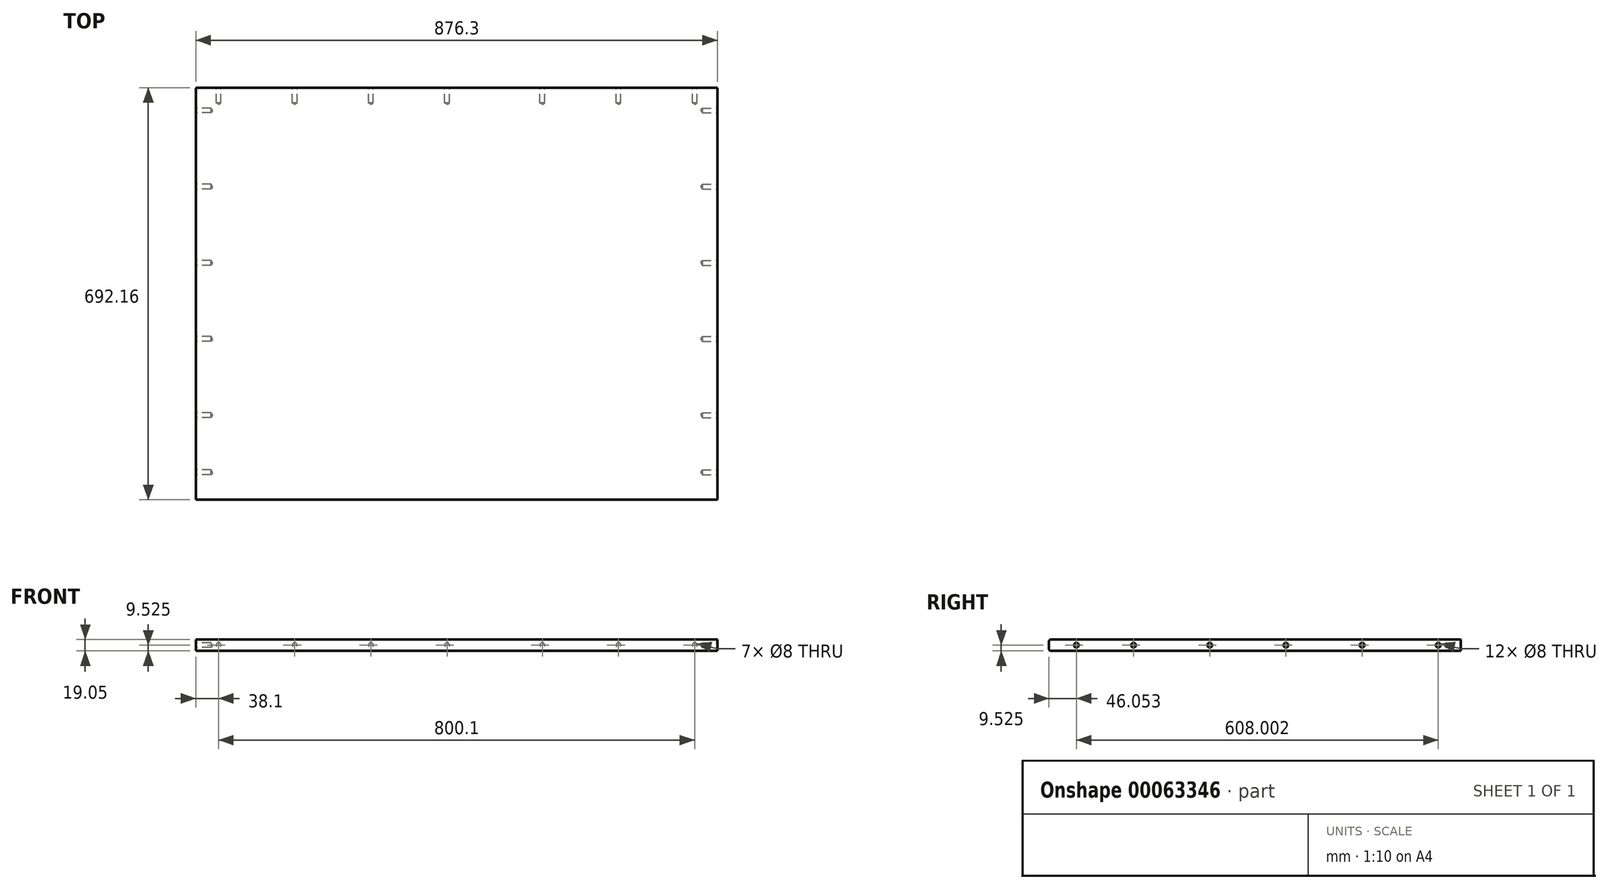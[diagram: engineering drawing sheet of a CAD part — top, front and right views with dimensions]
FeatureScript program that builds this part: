
annotation { "Feature Type Name" : "Feature", "Feature Type Description" : "" }
export const myFeature = defineFeature(function(context is Context, id is Id, definition is map)
    precondition{}
    {
        {
            var Q0;
            Q0=qCreatedBy(makeId("Top.planeOp"),FACE);
            var sketch = newSketch(context, id + "F0", { "sketchPlane" : qUnion([Q0])});
            skLineSegment(sketch, "E0.rect.bottom", {"start": v(438.15, -346.08) * mm, "end": v(-438.15, -346.08) * mm});
            skLineSegment(sketch, "E0.rect.top", {"start": v(438.15, 346.08) * mm, "end": v(-438.15, 346.07) * mm});
            skLineSegment(sketch, "E0.rect.left", {"start": v(438.15, -346.08) * mm, "end": v(438.15, 346.08) * mm});
            skLineSegment(sketch, "E0.rect.right", {"start": v(-438.15, -346.08) * mm, "end": v(-438.15, 346.08) * mm});
            skPoint(sketch, "E0.rect.middle", {"position": v(0, 0) * mm});
            skSolve(sketch);
        }
        {
            var Q0;
            Q0 = qSketchRegion(id + "F0", true);
            extrude(context, id + "F1", {"entities" : qUnion([Q0]), "depth" : 19.05 * mm});
        }
        {
            var Q0;
            Q0=makeQuery(id+"F1.opExtrude","CAP_EDGE",EDGE,{"disambiguationData":[OSD([sQuery(id+"F0.wireOp",EDGE,"E0.rect.bottom")])],"isStart":false});
            var Q1;
            Q1=makeQuery(id+"F1.opExtrude","CAP_EDGE",EDGE,{"disambiguationData":[OSD([sQuery(id+"F0.wireOp",EDGE,"E0.rect.bottom")])],"isStart":true});
            fillet(context, id + "F2", {"entities" : qUnion([Q0, Q1]), "radius" : 3.17 * mm, "tangentPropagation" : true, "allowEdgeOverflow" : false});
        }
        {
            var Q0;
            Q0=makeQuery(id+"F1.opExtrude","SWEPT_FACE",FACE,{"disambiguationData":[OSD([sQuery(id+"F0.wireOp",EDGE,"E0.rect.left")])]});
            var sketch = newSketch(context, id + "F3", { "sketchPlane" : qUnion([Q0])});
            skPoint(sketch, "E1", {"position": v(307.98, 9.53) * mm});
            skPoint(sketch, "E2", {"position": v(179.97, 9.53) * mm});
            skPoint(sketch, "E3", {"position": v(51.97, 9.53) * mm});
            skPoint(sketch, "E4", {"position": v(-76.03, 9.53) * mm});
            skPoint(sketch, "E5", {"position": v(-204.03, 9.53) * mm});
            skPoint(sketch, "E6", {"position": v(-300.03, 9.53) * mm});
            skSolve(sketch);
        }
        {
            var Q0;
            Q0=sQuery(id+"F3.wireOp",VERTEX,"E1");
            var Q1;
            Q1=sQuery(id+"F3.wireOp",VERTEX,"E2");
            var Q2;
            Q2=sQuery(id+"F3.wireOp",VERTEX,"E3");
            var Q3;
            Q3=sQuery(id+"F3.wireOp",VERTEX,"E4");
            var Q4;
            Q4=sQuery(id+"F3.wireOp",VERTEX,"E5");
            var Q5;
            Q5=sQuery(id+"F3.wireOp",VERTEX,"E6");
            var Q6;
            Q6=makeQuery(id+"F1.opExtrude","SWEPT_BODY",BODY,{"disambiguationData":[OSD([sQuery(id+"F0.wireOp",EDGE,"E0.rect.bottom"),sQuery(id+"F0.wireOp",EDGE,"E0.rect.top"),sQuery(id+"F0.wireOp",EDGE,"E0.rect.left"),sQuery(id+"F0.wireOp",EDGE,"E0.rect.right")])]});
            hole(context, id + "F4", {"style" : HoleStyle.SIMPLE, "holeDiameter" : 8 * mm, "endStyle" : HoleEndStyle.BLIND, "holeDepth" : 25.4 * mm, "locations" : qUnion([Q0, Q1, Q2, Q3, Q4, Q5]), "scope" : qUnion([Q6])});
        }
        {
            var Q0;
            Q0=makeQuery(id+"F1.opExtrude","SWEPT_FACE",FACE,{"disambiguationData":[OSD([sQuery(id+"F0.wireOp",EDGE,"E0.rect.right")])]});
            var sketch = newSketch(context, id + "F5", { "sketchPlane" : qUnion([Q0])});
            skPoint(sketch, "E7", {"position": v(300.03, 9.53) * mm});
            skPoint(sketch, "E8", {"position": v(204.03, 9.53) * mm});
            skPoint(sketch, "E9", {"position": v(76.03, 9.53) * mm});
            skPoint(sketch, "E10", {"position": v(-51.97, 9.53) * mm});
            skPoint(sketch, "E11", {"position": v(-179.97, 9.53) * mm});
            skPoint(sketch, "E12", {"position": v(-307.98, 9.53) * mm});
            skSolve(sketch);
        }
        {
            var Q0;
            Q0=sQuery(id+"F5.wireOp",VERTEX,"E12");
            var Q1;
            Q1=sQuery(id+"F5.wireOp",VERTEX,"E11");
            var Q2;
            Q2=sQuery(id+"F5.wireOp",VERTEX,"E10");
            var Q3;
            Q3=sQuery(id+"F5.wireOp",VERTEX,"E9");
            var Q4;
            Q4=sQuery(id+"F5.wireOp",VERTEX,"E8");
            var Q5;
            Q5=sQuery(id+"F5.wireOp",VERTEX,"E7");
            var Q6;
            Q6=makeQuery(id+"F1.opExtrude","SWEPT_BODY",BODY,{"disambiguationData":[OSD([sQuery(id+"F0.wireOp",EDGE,"E0.rect.bottom"),sQuery(id+"F0.wireOp",EDGE,"E0.rect.top"),sQuery(id+"F0.wireOp",EDGE,"E0.rect.left"),sQuery(id+"F0.wireOp",EDGE,"E0.rect.right")])]});
            hole(context, id + "F6", {"style" : HoleStyle.SIMPLE, "holeDiameter" : 8 * mm, "endStyle" : HoleEndStyle.BLIND, "holeDepth" : 25.4 * mm, "locations" : qUnion([Q0, Q1, Q2, Q3, Q4, Q5]), "scope" : qUnion([Q6])});
        }
        {
            var Q0;
            Q0=makeQuery(id+"F1.opExtrude","SWEPT_FACE",FACE,{"disambiguationData":[OSD([sQuery(id+"F0.wireOp",EDGE,"E0.rect.top")])]});
            var sketch = newSketch(context, id + "F7", { "sketchPlane" : qUnion([Q0])});
            skLineSegment(sketch, "E13", {"start": v(0, 19.05) * mm, "end": v(0, 0) * mm, "construction": true});
            skPoint(sketch, "E14", {"position": v(-400.05, 9.53) * mm});
            skPoint(sketch, "E15", {"position": v(-272.05, 9.53) * mm});
            skPoint(sketch, "E16", {"position": v(-144.05, 9.53) * mm});
            skPoint(sketch, "E17.MirrorP", {"position": v(144.05, 9.53) * mm});
            skPoint(sketch, "E18.MirrorP", {"position": v(272.05, 9.53) * mm});
            skPoint(sketch, "E19.MirrorP", {"position": v(400.05, 9.53) * mm});
            skPoint(sketch, "E20", {"position": v(16.05, 9.53) * mm});
            skSolve(sketch);
        }
        {
            var Q0;
            Q0=sQuery(id+"F7.wireOp",VERTEX,"E14");
            var Q1;
            Q1=sQuery(id+"F7.wireOp",VERTEX,"E15");
            var Q2;
            Q2=sQuery(id+"F7.wireOp",VERTEX,"E16");
            var Q3;
            Q3=sQuery(id+"F7.wireOp",VERTEX,"E20");
            var Q4;
            Q4=sQuery(id+"F7.wireOp",VERTEX,"E17.MirrorP");
            var Q5;
            Q5=sQuery(id+"F7.wireOp",VERTEX,"E18.MirrorP");
            var Q6;
            Q6=sQuery(id+"F7.wireOp",VERTEX,"E19.MirrorP");
            var Q7;
            Q7=makeQuery(id+"F1.opExtrude","SWEPT_BODY",BODY,{"disambiguationData":[OSD([sQuery(id+"F0.wireOp",EDGE,"E0.rect.bottom"),sQuery(id+"F0.wireOp",EDGE,"E0.rect.top"),sQuery(id+"F0.wireOp",EDGE,"E0.rect.left"),sQuery(id+"F0.wireOp",EDGE,"E0.rect.right")])]});
            hole(context, id + "F8", {"style" : HoleStyle.SIMPLE, "holeDiameter" : 8 * mm, "endStyle" : HoleEndStyle.BLIND, "holeDepth" : 25.4 * mm, "locations" : qUnion([Q0, Q1, Q2, Q3, Q4, Q5, Q6]), "scope" : qUnion([Q7])});
        }
    });
